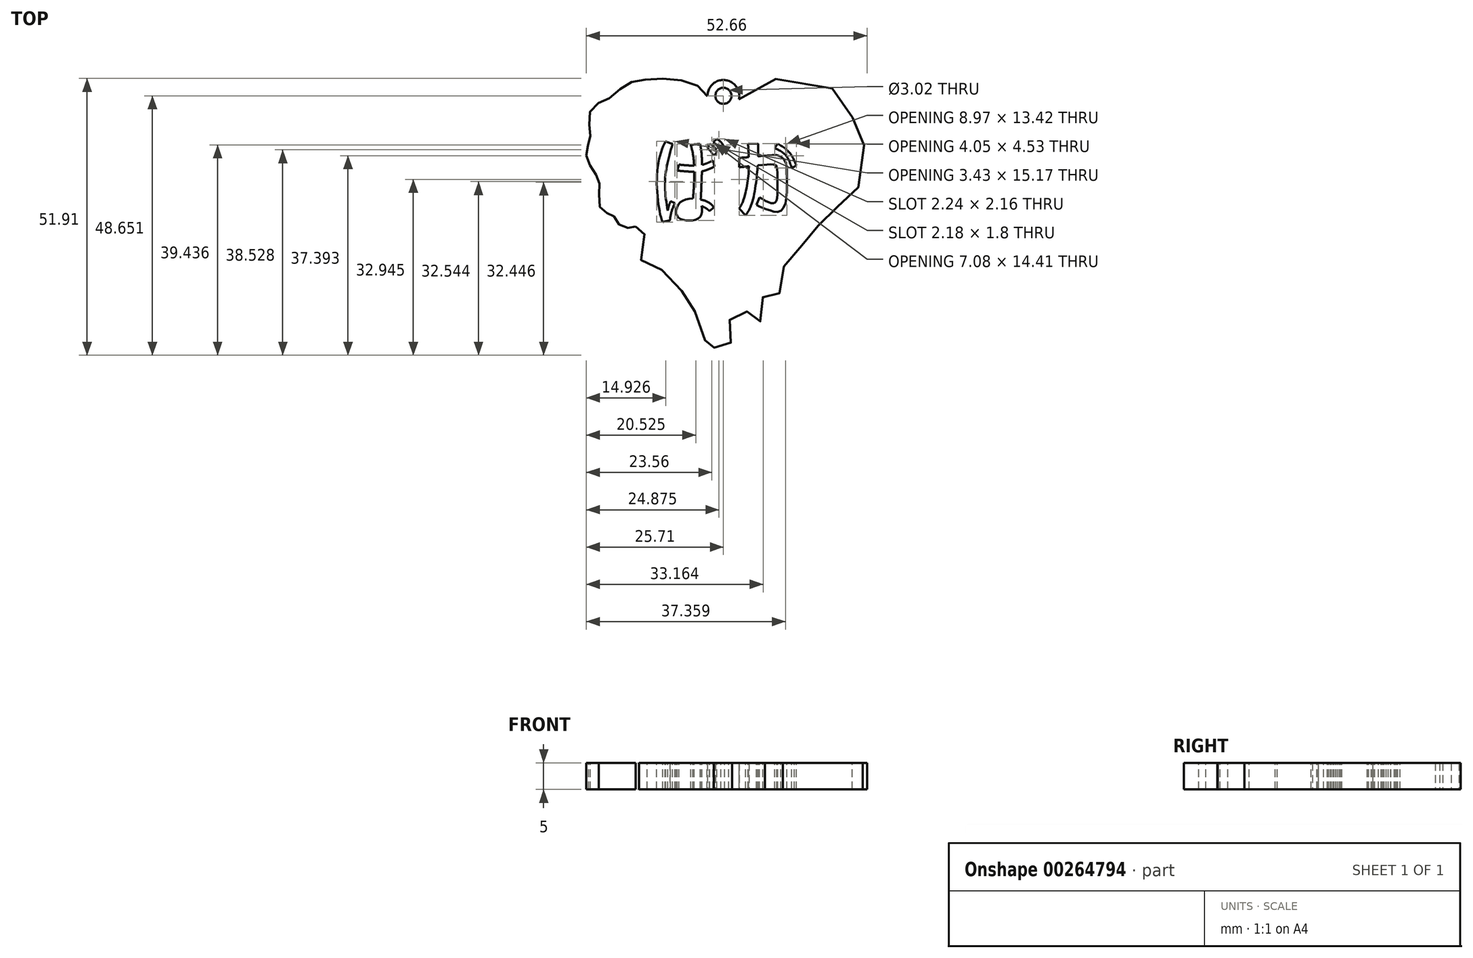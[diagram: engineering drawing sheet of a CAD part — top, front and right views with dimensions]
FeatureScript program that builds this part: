
annotation { "Feature Type Name" : "Feature", "Feature Type Description" : "" }
export const myFeature = defineFeature(function(context is Context, id is Id, definition is map)
    precondition{}
    {
        {
            var Q0;
            Q0=qCreatedBy(makeId("Top.planeOp"),FACE);
            var sketch = newSketch(context, id + "F0", { "sketchPlane" : qUnion([Q0])});
            skLineSegment(sketch, "E0", {"start": v(0.08, 15.96) * mm, "end": v(0.08, -29.04) * mm, "construction": true});
            skFitSpline(sketch, "E1", {"points": [v(0.08, 15.12) * mm, v(1.8, 15.96) * mm, v(5.58, 18.64) * mm, v(10.27, 20.57) * mm, v(19.75, 18.98) * mm, v(24.03, 15.96) * mm, v(24.45, 12.86) * mm, v(26.8, 11.1) * mm, v(26.13, 6.82) * mm, v(26.04, 2.12) * mm, v(23.27, -2.16) * mm, v(21.76, -2.5) * mm, v(21.1, -4.34) * mm, v(19.08, -6.1) * mm, v(17.82, -6.94) * mm, v(17.4, -9.03) * mm, v(15.64, -10.54) * mm, v(14.05, -10.96) * mm, v(13.55, -11.97) * mm, v(11.31, -14.7) * mm, v(10.84, -16.77) * mm, v(11.02, -19.08) * mm, v(9.42, -19.91) * mm, v(8.4, -19.08) * mm, v(7.52, -19.68) * mm, v(7.64, -22.23) * mm, v(7.7, -24.18) * mm, v(6.92, -24.96) * mm, v(6.21, -24.54) * mm, v(5.98, -25.01) * mm, v(5.09, -23.65) * mm, v(3.95, -23.12) * mm, v(3.15, -23.83) * mm, v(2.05, -24.06) * mm, v(1.07, -24.92) * mm, v(1.37, -27.18) * mm, v(1.6, -28.22) * mm, v(1.31, -29.31) * mm, v(0.68, -31) * mm, v(-1.46, -30.7) * mm, v(-1.93, -27.26) * mm, v(-2.64, -27.61) * mm, v(-3.35, -28.5) * mm, v(-4.3, -27.67) * mm, v(-5.2, -23.88) * mm, v(-5.67, -22.34) * mm, v(-6.74, -20.85) * mm, v(-7.62, -19.37) * mm, v(-10.41, -18.13) * mm, v(-11.48, -16) * mm, v(-12.13, -13.86) * mm, v(-14.5, -14.15) * mm, v(-15.75, -12.61) * mm, v(-15.51, -9.65) * mm, v(-15.04, -9) * mm, v(-14.33, -7.33) * mm, v(-14.5, -6.15) * mm, v(-16.46, -7.15) * mm], "startDerivative": vector(95.52, 38.59) * mm, "endDerivative": vector(-155.6, -97.2) * mm});
            skFitSpline(sketch, "E2", {"points": [v(-16.46, -7.15) * mm, v(-17.56, -7.42) * mm, v(-19.07, -7.15) * mm, v(-20.23, -5.85) * mm, v(-20.94, -4.84) * mm, v(-22.37, -4.47) * mm, v(-23.32, -2.82) * mm, v(-23.25, 0) * mm, v(-23.46, 1.56) * mm, v(-24.38, 3.32) * mm, v(-25.54, 5.33) * mm, v(-25.65, 7.1) * mm, v(-25.15, 9) * mm, v(-24.98, 10.83) * mm, v(-25.19, 13.83) * mm, v(-23.58, 15.97) * mm, v(-21.2, 17.06) * mm, v(-18.3, 19.45) * mm, v(-15.24, 20.33) * mm, v(-9.5, 20.5) * mm, v(-4.33, 18.86) * mm, v(-2.15, 16.14) * mm, v(-0.7, 15.1) * mm, v(0.08, 15.12) * mm], "startDerivative": vector(-33.79, -11.1) * mm, "endDerivative": vector(28.69, 5.55) * mm});
            skFitSpline(sketch, "E3", {"points": [v(-15.54, 7.18) * mm, v(-16.93, 6.43) * mm, v(-18.22, 6.03) * mm, v(-18.97, 4.49) * mm, v(-17.48, 2.5) * mm, v(-15.18, 1.6) * mm, v(-13.54, 0) * mm, v(-10.45, 0) * mm, v(-8.2, 0.55) * mm, v(-7.81, 0.5) * mm, v(-7.52, 0.56) * mm, v(-7.36, 1.37) * mm, v(-6.93, 1.67) * mm, v(-6.3, 2.5) * mm, v(-5.9, 2.96) * mm, v(-5.21, 3.13) * mm, v(-3.7, 4.49) * mm, v(-3.46, 7.08) * mm, v(-3.3, 9.72) * mm, v(-4.6, 11.37) * mm, v(-6.9, 10.92) * mm, v(-8.9, 8.87) * mm, v(-10.99, 8.82) * mm, v(-12.63, 8.57) * mm, v(-14.5, 8.18) * mm, v(-15.54, 7.18) * mm]});
            skFitSpline(sketch, "E4", {"points": [v(5.9, 10.84) * mm, v(4.72, 9.72) * mm, v(4.49, 8.06) * mm, v(5.44, 7.34) * mm, v(5.2, 5.8) * mm, v(6.27, 4.14) * mm, v(8.22, 3.6) * mm, v(9.82, 1.53) * mm, v(11.13, -0.54) * mm, v(12.61, -0.54) * mm, v(15.46, 1.06) * mm, v(17.47, 1.65) * mm, v(17.89, 4.2) * mm, v(15.93, 4.32) * mm, v(15.52, 7.17) * mm, v(14.92, 8.06) * mm, v(12.61, 8.47) * mm, v(11.25, 10.66) * mm, v(9.65, 10.66) * mm, v(6.86, 10.84) * mm, v(5.9, 10.84) * mm]});
            skCircle(sketch, "E5", {"center": v(0, 17.36) * mm, "radius": 2.97 * mm});
            skCircle(sketch, "E6", {"center": v(0, 17.36) * mm, "radius": 1.5 * mm});
            skSolve(sketch);
        }
        {
            var Q0;
            Q0=makeQuery(id+"F0.imprint","IMPRINT",FACE,{"disambiguationData":[TD([[makeQuery(id+"F0.imprint","IMPRINT",EDGE,{"derivedFrom":sQuery(id+"F0.wireOp",EDGE,"E1")}),-1.0]])]});
            var Q1;
            Q1=makeQuery(id+"F0.imprint","IMPRINT",FACE,{"disambiguationData":[TD([[makeQuery(id+"F0.imprint","IMPRINT",EDGE,{"derivedFrom":sQuery(id+"F0.wireOp",EDGE,"E3")}),-1.0]])]});
            var Q2;
            Q2=makeQuery(id+"F0.imprint","IMPRINT",FACE,{"disambiguationData":[TD([[makeQuery(id+"F0.imprint","IMPRINT",EDGE,{"derivedFrom":sQuery(id+"F0.wireOp",EDGE,"E6")}),-1.0]])]});
            var Q3;
            Q3=makeQuery(id+"F0.imprint","IMPRINT",FACE,{"disambiguationData":[TD([[makeQuery(id+"F0.imprint","IMPRINT",EDGE,{"derivedFrom":sQuery(id+"F0.wireOp",EDGE,"E3")}),1.0]])]});
            var Q4;
            Q4=makeQuery(id+"F0.imprint","IMPRINT",FACE,{"disambiguationData":[TD([[makeQuery(id+"F0.imprint","IMPRINT",EDGE,{"derivedFrom":sQuery(id+"F0.wireOp",EDGE,"E4")}),1.0]])]});
            extrude(context, id + "F1", {"entities" : qUnion([Q0, Q1, Q2, Q3, Q4]), "depth" : 5 * mm, "offsetDistance" : 25 * mm});
        }
        {
            var Q0;
            Q0=makeQuery(id+"F1.opExtrude","CAP_FACE",FACE,{"disambiguationData":[OSD([sQuery(id+"F0.wireOp",EDGE,"E1"),sQuery(id+"F0.wireOp",EDGE,"E2"),sQuery(id+"F0.wireOp",EDGE,"E5"),sQuery(id+"F0.wireOp",EDGE,"E6")])],"isStart":false});
            var sketch = newSketch(context, id + "F2", { "sketchPlane" : qUnion([Q0])});
            skLineSegment(sketch, "E7", {"start": v(-13.16, -6.33) * mm, "end": v(16.74, -6.33) * mm, "construction": true});
            skLineSegment(sketch, "E8", {"start": v(16.74, -6.33) * mm, "end": v(16.74, 9.26) * mm, "construction": true});
            skLineSegment(sketch, "E9", {"start": v(16.74, 9.26) * mm, "end": v(-13.16, 9.26) * mm, "construction": true});
            skLineSegment(sketch, "E10", {"start": v(-13.16, 9.26) * mm, "end": v(-13.16, -6.33) * mm, "construction": true});
            skFitSpline(sketch, "E11", {"points": [v(-10.8, 8.84) * mm, v(-11.93, 6.04) * mm, v(-12.5, 1.16) * mm, v(-12.07, -3.77) * mm, v(-11.36, -6.33) * mm], "startDerivative": vector(-6.02, -9.28) * mm, "endDerivative": vector(4.94, -9.57) * mm});
            skFitSpline(sketch, "E12", {"points": [v(-10.8, 8.84) * mm, v(-10.28, 8.58) * mm, v(-9.54, 8.35) * mm], "startDerivative": vector(1.05, -0.57) * mm, "endDerivative": vector(1.44, -0.4) * mm});
            skFitSpline(sketch, "E13", {"points": [v(-9.54, 8.35) * mm, v(-10.95, 1.3) * mm, v(-10.04, -6.07) * mm], "startDerivative": vector(-3.92, -13.91) * mm, "endDerivative": vector(2.94, -13.12) * mm});
            skFitSpline(sketch, "E14", {"points": [v(-10.04, -6.07) * mm, v(-11.36, -6.33) * mm], "startDerivative": vector(-1.2, -0.1) * mm, "endDerivative": vector(-1.54, -0.47) * mm});
            skFitSpline(sketch, "E15", {"points": [v(-10.04, -6.07) * mm, v(-9.7, -4.26) * mm, v(-9.07, -2.75) * mm], "startDerivative": vector(0.48, 3.62) * mm, "endDerivative": vector(1.47, 3) * mm});
            skFitSpline(sketch, "E16", {"points": [v(-9.07, -2.75) * mm, v(-9.9, -2.42) * mm], "startDerivative": vector(-0.82, 0.34) * mm, "endDerivative": vector(-0.82, 0.34) * mm});
            skFitSpline(sketch, "E17", {"points": [v(-9.9, -2.42) * mm, v(-10.04, -2.75) * mm, v(-10.44, -4.17) * mm], "startDerivative": vector(-0.43, -0.82) * mm, "endDerivative": vector(-0.48, -2.66) * mm});
            skFitSpline(sketch, "E18", {"points": [v(-6.12, 8.17) * mm, v(-5.62, 5.8) * mm, v(-5.5, 1.3) * mm, v(-5.95, -4.9) * mm], "startDerivative": vector(2.32, -8.67) * mm, "endDerivative": vector(-1.4, -15.69) * mm});
            skFitSpline(sketch, "E19", {"points": [v(-5.95, -4.9) * mm, v(-4.36, -4.9) * mm], "startDerivative": vector(1.3, 0) * mm, "endDerivative": vector(1.3, 0) * mm});
            skFitSpline(sketch, "E20", {"points": [v(-4.36, -4.9) * mm, v(-4.12, 0.56) * mm, v(-4.05, 5.87) * mm, v(-4.36, 8.36) * mm], "startDerivative": vector(0.46, 15.82) * mm, "endDerivative": vector(-2.5, 9.05) * mm, "construction": true});
            skFitSpline(sketch, "E21", {"points": [v(-4.36, 8.36) * mm, v(-6.12, 8.17) * mm], "startDerivative": vector(-1.47, -0.2) * mm, "endDerivative": vector(-1.47, -0.2) * mm});
            skFitSpline(sketch, "E22", {"points": [v(-4.36, -4.9) * mm, v(-5.37, -5.7) * mm, v(-7.44, -5.83) * mm, v(-8.67, -4.9) * mm, v(-8.37, -3.2) * mm, v(-7.14, -2.26) * mm, v(-5.72, -2.22) * mm, v(-4.28, -2.84) * mm, v(-3.01, -3.78) * mm], "startDerivative": vector(-6.42, -6.97) * mm, "endDerivative": vector(10.4, -8.5) * mm, "construction": true});
            skFitSpline(sketch, "E23", {"points": [v(-3.01, -3.78) * mm, v(-3.74, -4.55) * mm], "startDerivative": vector(-0.73, -0.77) * mm, "endDerivative": vector(-0.73, -0.77) * mm});
            skFitSpline(sketch, "E24", {"points": [v(-3.74, -4.55) * mm, v(-4.33, -4) * mm, v(-5.81, -3.31) * mm, v(-6.75, -3.25) * mm, v(-7.54, -4) * mm, v(-7.18, -4.56) * mm, v(-5.91, -4.42) * mm], "startDerivative": vector(-4.28, 4.04) * mm, "endDerivative": vector(9.33, 5.88) * mm, "construction": true});
            skFitSpline(sketch, "E25", {"points": [v(-8.33, 4.46) * mm, v(-5.5, 4.26) * mm, v(-3.73, 4.49) * mm, v(-1.93, 5.22) * mm], "startDerivative": vector(7.87, -0.77) * mm, "endDerivative": vector(5.76, 2.67) * mm});
            skFitSpline(sketch, "E26", {"points": [v(-8.33, 4.46) * mm, v(-8.66, 3.33) * mm], "startDerivative": vector(-0.34, -1.13) * mm, "endDerivative": vector(-0.34, -1.13) * mm});
            skFitSpline(sketch, "E27", {"points": [v(-8.66, 3.33) * mm, v(-5.47, 3.1) * mm, v(-3.5, 3.33) * mm, v(-1.65, 4.1) * mm], "startDerivative": vector(8.74, -0.85) * mm, "endDerivative": vector(6.05, 2.86) * mm});
            skFitSpline(sketch, "E28", {"points": [v(-1.65, 4.1) * mm, v(-1.93, 5.22) * mm], "startDerivative": vector(-0.28, 1.13) * mm, "endDerivative": vector(-0.28, 1.13) * mm});
            skFitSpline(sketch, "E29", {"points": [v(-4.36, -4.9) * mm, v(-5.37, -5.7) * mm, v(-7.44, -5.83) * mm, v(-8.67, -4.9) * mm, v(-8.37, -3.2) * mm, v(-7.14, -2.26) * mm, v(-5.5, -1.95) * mm, v(-4.25, -2.1) * mm, v(-3.16, -2.45) * mm, v(-2.1, -3.2) * mm, v(-1.8, -3.62) * mm], "startDerivative": vector(-7.64, -8.88) * mm, "endDerivative": vector(3.46, -6.08) * mm});
            skFitSpline(sketch, "E30", {"points": [v(-1.8, -3.62) * mm, v(-2.6, -4.24) * mm], "startDerivative": vector(-0.79, -0.62) * mm, "endDerivative": vector(-0.79, -0.62) * mm});
            skFitSpline(sketch, "E31", {"points": [v(-2.6, -4.24) * mm, v(-3.46, -3.62) * mm, v(-4.3, -3.2) * mm], "startDerivative": vector(-1.64, 1.3) * mm, "endDerivative": vector(-1.71, 0.72) * mm});
            skFitSpline(sketch, "E32", {"points": [v(-4.36, 8.36) * mm, v(-4.05, 5.87) * mm, v(-4.12, 0.56) * mm, v(-4.25, -2.1) * mm], "startDerivative": vector(1.32, -7.53) * mm, "endDerivative": vector(-0.4, -7.9) * mm});
            skFitSpline(sketch, "E33", {"points": [v(-4.36, -4.9) * mm, v(-4.25, -4.48) * mm, v(-4.25, -3.61) * mm, v(-4.3, -3.2) * mm], "startDerivative": vector(0.47, 1.25) * mm, "endDerivative": vector(-0.2, 1.27) * mm});
            skArc(sketch, "E34", {"start": v(-1.25, 6.67) * mm, "mid": v(-1.66, 7.7) * mm, "end": v(-2.58, 8.33) * mm});
            skFitSpline(sketch, "E35", {"points": [v(-1.25, 6.67) * mm, v(-1.87, 6.15) * mm], "startDerivative": vector(-0.62, -0.52) * mm, "endDerivative": vector(-0.62, -0.52) * mm});
            skFitSpline(sketch, "E36", {"points": [v(-2.58, 8.33) * mm, v(-3.05, 7.57) * mm], "startDerivative": vector(-0.47, -0.76) * mm, "endDerivative": vector(-0.47, -0.76) * mm});
            skArc(sketch, "E37", {"start": v(-1.87, 6.15) * mm, "mid": v(-2.36, 6.94) * mm, "end": v(-3.05, 7.57) * mm});
            skArc(sketch, "E38", {"start": v(-0.5, 7.03) * mm, "mid": v(-1.05, 7.95) * mm, "end": v(-1.91, 8.62) * mm});
            skArc(sketch, "E39", {"start": v(0.24, 7.5) * mm, "mid": v(-0.32, 8.51) * mm, "end": v(-1.2, 9.26) * mm});
            skFitSpline(sketch, "E40", {"points": [v(-1.2, 9.26) * mm, v(-1.91, 8.62) * mm], "startDerivative": vector(-0.71, -0.65) * mm, "endDerivative": vector(-0.71, -0.65) * mm});
            skFitSpline(sketch, "E41", {"points": [v(-0.5, 7.03) * mm, v(0.24, 7.5) * mm], "startDerivative": vector(0.73, 0.47) * mm, "endDerivative": vector(0.73, 0.47) * mm});
            skFitSpline(sketch, "E42", {"points": [v(-4.22, -1.58) * mm, v(-4.03, -3.6) * mm, v(-4.05, -4.62) * mm, v(-4.36, -5.36) * mm, v(-5.18, -5.88) * mm, v(-6.23, -6.05) * mm, v(-6.4, -6.05) * mm, v(-7.27, -5.97) * mm, v(-8.11, -5.74) * mm, v(-8.6, -5.26) * mm, v(-8.85, -4.5) * mm, v(-8.53, -3.2) * mm, v(-7.78, -2.4) * mm, v(-6.48, -1.95) * mm, v(-4.97, -1.95) * mm, v(-4.6, -2.04) * mm], "startDerivative": vector(2.38, -22.28) * mm, "endDerivative": vector(7.06, -2.12) * mm});
            skFitSpline(sketch, "E43", {"points": [v(4.63, 8.34) * mm, v(4.52, 4.27) * mm, v(3, -2.08) * mm, v(0.87, -4.98) * mm], "startDerivative": vector(-0.07, -11.9) * mm, "endDerivative": vector(-7.87, -8.24) * mm, "construction": true});
            skPoint(sketch, "E44.1.internal.snap0", {"position": v(1.8, -6.33) * mm});
            skFitSpline(sketch, "E44", {"points": [v(0.87, -4.98) * mm, v(1.8, -5.83) * mm], "startDerivative": vector(0.92, -0.85) * mm, "endDerivative": vector(0.92, -0.85) * mm});
            skFitSpline(sketch, "E45", {"points": [v(1.8, -5.83) * mm, v(4.33, -2.94) * mm, v(5.8, 4.22) * mm, v(5.9, 8.48) * mm], "startDerivative": vector(9.65, 7.85) * mm, "endDerivative": vector(-0.14, 12.43) * mm, "construction": true});
            skFitSpline(sketch, "E46", {"points": [v(5.9, 8.48) * mm, v(4.63, 8.34) * mm], "startDerivative": vector(-1.18, -0.14) * mm, "endDerivative": vector(-1.18, -0.14) * mm, "construction": true});
            skFitSpline(sketch, "E47", {"points": [v(2.97, 5.7) * mm, v(4.61, 5.8) * mm, v(5.89, 5.93) * mm, v(8.2, 6.17) * mm, v(10.5, 6.11) * mm, v(11.72, 4.7) * mm, v(11.91, 1.1) * mm, v(11.66, -2.7) * mm, v(10.57, -4.33) * mm, v(8.42, -3.96) * mm, v(6.8, -2.42) * mm], "startDerivative": vector(19.2, 1.37) * mm, "endDerivative": vector(-10.73, 17.37) * mm, "construction": true});
            skFitSpline(sketch, "E48", {"points": [v(6.8, -2.42) * mm, v(7.94, -1.93) * mm], "startDerivative": vector(1.23, 0.8) * mm, "endDerivative": vector(1.23, 0.8) * mm, "construction": true});
            skFitSpline(sketch, "E49", {"points": [v(7.94, -1.93) * mm, v(9.85, -2.83) * mm, v(10.48, -2.42) * mm, v(10.68, 1) * mm, v(10.5, 4.17) * mm, v(9.78, 4.46) * mm, v(5.8, 4.22) * mm], "startDerivative": vector(6.91, -12.73) * mm, "endDerivative": vector(-20.39, -1.62) * mm, "construction": true});
            skFitSpline(sketch, "E50", {"points": [v(2.97, 5.7) * mm, v(2.97, 4.27) * mm], "startDerivative": vector(0, -1.37) * mm, "endDerivative": vector(0, -1.37) * mm});
            skFitSpline(sketch, "E51", {"points": [v(2.97, 4.27) * mm, v(4.52, 4.27) * mm], "startDerivative": vector(1.28, 0) * mm, "endDerivative": vector(1.28, 0) * mm});
            skFitSpline(sketch, "E52", {"points": [v(10.02, 8.16) * mm, v(11.47, 7.22) * mm, v(12.54, 5.98) * mm, v(13.34, 4.07) * mm], "startDerivative": vector(4.64, -2.7) * mm, "endDerivative": vector(2, -5.68) * mm});
            skFitSpline(sketch, "E53", {"points": [v(10.02, 8.16) * mm, v(9.62, 7.56) * mm], "startDerivative": vector(-0.4, -0.6) * mm, "endDerivative": vector(-0.4, -0.6) * mm});
            skFitSpline(sketch, "E54", {"points": [v(9.62, 7.56) * mm, v(11.13, 6.72) * mm, v(12.1, 5.65) * mm, v(12.8, 3.84) * mm], "startDerivative": vector(4.78, -2.32) * mm, "endDerivative": vector(1.73, -5.46) * mm});
            skFitSpline(sketch, "E55", {"points": [v(12.8, 3.84) * mm, v(13.34, 4.07) * mm], "startDerivative": vector(0.54, 0.23) * mm, "endDerivative": vector(0.54, 0.23) * mm});
            skFitSpline(sketch, "E56", {"points": [v(13.34, 4.07) * mm, v(13.68, 4.32) * mm], "startDerivative": vector(0.33, 0.25) * mm, "endDerivative": vector(0.33, 0.25) * mm});
            skFitSpline(sketch, "E57", {"points": [v(13.68, 4.32) * mm, v(12.8, 6.15) * mm, v(11.68, 7.39) * mm, v(10.19, 8.37) * mm], "startDerivative": vector(-2.25, 5.53) * mm, "endDerivative": vector(-4.74, 2.8) * mm});
            skFitSpline(sketch, "E58", {"points": [v(10.19, 8.37) * mm, v(10.02, 8.16) * mm], "startDerivative": vector(-0.16, -0.2) * mm, "endDerivative": vector(-0.16, -0.2) * mm});
            skFitSpline(sketch, "E59", {"points": [v(9.45, 4.46) * mm, v(10.02, 3.96) * mm, v(10.14, 0.9) * mm, v(9.98, -2.28) * mm, v(9.32, -2.8) * mm], "startDerivative": vector(4.1, -2.01) * mm, "endDerivative": vector(-4.46, -1.87) * mm, "construction": true});
            skFitSpline(sketch, "E60", {"points": [v(9.32, -2.8) * mm, v(7.97, -2.36) * mm, v(6.75, -1.68) * mm], "startDerivative": vector(-2.76, 0.73) * mm, "endDerivative": vector(-2.38, 1.49) * mm, "construction": true});
            skFitSpline(sketch, "E61", {"points": [v(6.75, -1.68) * mm, v(6.2, -3.12) * mm], "startDerivative": vector(-0.56, -1.43) * mm, "endDerivative": vector(-0.56, -1.43) * mm, "construction": true});
            skFitSpline(sketch, "E62", {"points": [v(6.2, -3.12) * mm, v(7.5, -3.74) * mm, v(8.97, -4.22) * mm], "startDerivative": vector(2.17, -1.42) * mm, "endDerivative": vector(3, -1.2) * mm, "construction": true});
            skFitSpline(sketch, "E63", {"points": [v(2.97, 5.7) * mm, v(5.89, 5.93) * mm, v(8.2, 6.17) * mm, v(10.5, 6.11) * mm, v(11.72, 4.7) * mm, v(11.91, 1.1) * mm, v(11.66, -2.7) * mm, v(10.57, -4.33) * mm, v(8.97, -4.22) * mm, v(7.5, -3.74) * mm, v(6.2, -3.12) * mm], "startDerivative": vector(26.47, 2.28) * mm, "endDerivative": vector(-16.18, 8.31) * mm});
            skFitSpline(sketch, "E64", {"points": [v(6.2, -3.12) * mm, v(6.75, -1.68) * mm], "startDerivative": vector(0.56, 1.43) * mm, "endDerivative": vector(0.56, 1.43) * mm});
            skFitSpline(sketch, "E65", {"points": [v(6.75, -1.68) * mm, v(7.97, -2.36) * mm, v(9.32, -2.8) * mm, v(9.98, -2.28) * mm, v(10.14, 0.9) * mm, v(10.02, 3.96) * mm, v(9.45, 4.46) * mm, v(5.8, 4.22) * mm], "startDerivative": vector(9.4, -5.5) * mm, "endDerivative": vector(-22.2, -2.9) * mm});
            skFitSpline(sketch, "E66", {"points": [v(6.53, 8.37) * mm, v(6.55, 5.99) * mm, v(6.45, 4.3) * mm, v(5.48, -2.38) * mm, v(4.19, -5.06) * mm], "startDerivative": vector(0.2, -12.04) * mm, "endDerivative": vector(-5.84, -8.77) * mm});
            skFitSpline(sketch, "E67", {"points": [v(6.53, 8.37) * mm, v(4.63, 8.34) * mm], "startDerivative": vector(-1.82, -0.02) * mm, "endDerivative": vector(-1.82, -0.02) * mm});
            skFitSpline(sketch, "E68", {"points": [v(4.63, 8.34) * mm, v(4.63, 1.7) * mm, v(3.52, -2.8) * mm, v(2.97, -3.8) * mm], "startDerivative": vector(1.04, -15.91) * mm, "endDerivative": vector(-2.8, -4.44) * mm});
            skFitSpline(sketch, "E69", {"points": [v(2.97, -3.8) * mm, v(4.19, -5.06) * mm], "startDerivative": vector(1.22, -1.26) * mm, "endDerivative": vector(1.22, -1.26) * mm});
            skFitSpline(sketch, "E70", {"points": [v(5.8, 4.22) * mm, v(4.78, 4.13) * mm, v(3, 3.96) * mm], "startDerivative": vector(-2.2, -0.2) * mm, "endDerivative": vector(-3.36, -0.32) * mm});
            skFitSpline(sketch, "E71", {"points": [v(3, 3.96) * mm, v(2.97, 4.27) * mm], "startDerivative": vector(-0.02, 0.3) * mm, "endDerivative": vector(-0.02, 0.3) * mm});
            skSolve(sketch);
        }
        {
            var Q0;
            Q0=makeQuery(id+"F2.imprint","IMPRINT",FACE,{"disambiguationData":[TD([[makeQuery(id+"F2.imprint","IMPRINT",EDGE,{"derivedFrom":sQuery(id+"F2.wireOp",EDGE,"E11")}),1.0]])]});
            var Q1;
            {var subQ0=sQuery(id+"F2.wireOp",EDGE,"E15");Q1=makeQuery(id+"F2.imprint","IMPRINT",FACE,{"disambiguationData":[TD([[makeQuery(id+"F2.imprint","IMPRINT",EDGE,{"derivedFrom":subQ0}),1.0]])]});}
            var Q2;
            {var subQ0=sQuery(id+"F2.wireOp",EDGE,"E24");var subQ1=sQuery(id+"F2.wireOp",EDGE,"E18");var subQ2=makeQuery(id+"F2.imprint","INTERSECT",VERTEX,{"disambiguationData":[OD(0.0)],"derivedFrom":[subQ1,subQ0]});Q2=makeQuery(id+"F2.imprint","IMPRINT",FACE,{"disambiguationData":[TD([[makeQuery(id+"F2.imprint","IMPRINT",EDGE,{"disambiguationData":[TD([[subQ2,1.0]])],"derivedFrom":subQ1}),-1.0]])]});}
            var Q3;
            {var subQ0=sQuery(id+"F2.wireOp",EDGE,"E19");Q3=makeQuery(id+"F2.imprint","IMPRINT",FACE,{"disambiguationData":[TD([[makeQuery(id+"F2.imprint","IMPRINT",EDGE,{"derivedFrom":subQ0}),-1.0]])]});}
            var Q4;
            {var subQ1=sQuery(id+"F2.wireOp",EDGE,"E19");Q4=makeQuery(id+"F2.imprint","IMPRINT",FACE,{"disambiguationData":[TD([[makeQuery(id+"F2.imprint","IMPRINT",EDGE,{"derivedFrom":subQ1}),1.0]])]});}
            var Q5;
            {var subQ0=sQuery(id+"F2.wireOp",EDGE,"E22");var subQ1=sQuery(id+"F2.wireOp",EDGE,"E18");var subQ2=makeQuery(id+"F2.imprint","INTERSECT",VERTEX,{"derivedFrom":[subQ1,subQ0]});Q5=makeQuery(id+"F2.imprint","IMPRINT",FACE,{"disambiguationData":[TD([[makeQuery(id+"F2.imprint","IMPRINT",EDGE,{"disambiguationData":[TD([[subQ2,-1.0]])],"derivedFrom":subQ1}),1.0]])]});}
            var Q6;
            {var subQ5=sQuery(id+"F2.wireOp",EDGE,"E23");Q6=makeQuery(id+"F2.imprint","IMPRINT",FACE,{"disambiguationData":[TD([[makeQuery(id+"F2.imprint","IMPRINT",EDGE,{"derivedFrom":subQ5}),-1.0]])]});}
            var Q7;
            {var subQ0=sQuery(id+"F2.wireOp",EDGE,"E27");var subQ1=sQuery(id+"F2.wireOp",EDGE,"E18");var subQ2=makeQuery(id+"F2.imprint","INTERSECT",VERTEX,{"derivedFrom":[subQ1,subQ0]});Q7=makeQuery(id+"F2.imprint","IMPRINT",FACE,{"disambiguationData":[TD([[makeQuery(id+"F2.imprint","IMPRINT",EDGE,{"disambiguationData":[TD([[subQ2,-1.0]])],"derivedFrom":subQ1}),1.0]])]});}
            var Q8;
            {var subQ0=sQuery(id+"F2.wireOp",EDGE,"E25");var subQ1=sQuery(id+"F2.wireOp",EDGE,"E18");var subQ2=makeQuery(id+"F2.imprint","INTERSECT",VERTEX,{"derivedFrom":[subQ1,subQ0]});Q8=makeQuery(id+"F2.imprint","IMPRINT",FACE,{"disambiguationData":[TD([[makeQuery(id+"F2.imprint","IMPRINT",EDGE,{"disambiguationData":[TD([[subQ2,-1.0]])],"derivedFrom":subQ1}),1.0]])]});}
            var Q9;
            {var subQ5=sQuery(id+"F2.wireOp",EDGE,"E26");Q9=makeQuery(id+"F2.imprint","IMPRINT",FACE,{"disambiguationData":[TD([[makeQuery(id+"F2.imprint","IMPRINT",EDGE,{"derivedFrom":subQ5}),1.0]])]});}
            var Q10;
            {var subQ0=sQuery(id+"F2.wireOp",EDGE,"E21");Q10=makeQuery(id+"F2.imprint","IMPRINT",FACE,{"disambiguationData":[TD([[makeQuery(id+"F2.imprint","IMPRINT",EDGE,{"derivedFrom":subQ0}),1.0]])]});}
            var Q11;
            {var subQ5=sQuery(id+"F2.wireOp",EDGE,"E28");Q11=makeQuery(id+"F2.imprint","IMPRINT",FACE,{"disambiguationData":[TD([[makeQuery(id+"F2.imprint","IMPRINT",EDGE,{"derivedFrom":subQ5}),1.0]])]});}
            var Q12;
            {var subQ1=sQuery(id+"F2.wireOp",EDGE,"E30");Q12=makeQuery(id+"F2.imprint","IMPRINT",FACE,{"disambiguationData":[TD([[makeQuery(id+"F2.imprint","IMPRINT",EDGE,{"derivedFrom":subQ1}),-1.0]])]});}
            var Q13;
            Q13=makeQuery(id+"F2.imprint","IMPRINT",FACE,{"disambiguationData":[TD([[makeQuery(id+"F2.imprint","IMPRINT",EDGE,{"derivedFrom":sQuery(id+"F2.wireOp",EDGE,"b741c950-454b-47e5-acc8-c98bc9226f96")}),1.0]])]});
            var Q14;
            Q14=makeQuery(id+"F2.imprint","IMPRINT",FACE,{"disambiguationData":[TD([[makeQuery(id+"F2.imprint","IMPRINT",EDGE,{"derivedFrom":sQuery(id+"F2.wireOp",EDGE,"d5f50271-82d2-4fe2-802b-595531122f13")}),1.0]])]});
            var Q15;
            Q15=makeQuery(id+"F2.imprint","IMPRINT",FACE,{"disambiguationData":[TD([[makeQuery(id+"F2.imprint","IMPRINT",EDGE,{"derivedFrom":sQuery(id+"F2.wireOp",EDGE,"E34")}),1.0]])]});
            var Q16;
            Q16=makeQuery(id+"F2.imprint","IMPRINT",FACE,{"disambiguationData":[TD([[makeQuery(id+"F2.imprint","IMPRINT",EDGE,{"derivedFrom":sQuery(id+"F2.wireOp",EDGE,"E38")}),-1.0]])]});
            var Q17;
            {var subQ0=sQuery(id+"F2.wireOp",EDGE,"E33");Q17=makeQuery(id+"F2.imprint","IMPRINT",FACE,{"disambiguationData":[TD([[makeQuery(id+"F2.imprint","IMPRINT",EDGE,{"derivedFrom":subQ0}),-1.0]])]});}
            extrude(context, id + "F3", {"entities" : qUnion([Q0, Q1, Q2, Q3, Q4, Q5, Q6, Q7, Q8, Q9, Q10, Q11, Q12, Q13, Q14, Q15, Q16, Q17]), "operationType" : NewBodyOperationType.REMOVE, "oppositeDirection" : true, "depth" : 25 * mm, "offsetDistance" : 25 * mm});
        }
        {
            var Q0;
            {var subQ1=sQuery(id+"F2.wireOp",EDGE,"E44");Q0=makeQuery(id+"F2.imprint","IMPRINT",FACE,{"disambiguationData":[TD([[makeQuery(id+"F2.imprint","IMPRINT",EDGE,{"derivedFrom":subQ1}),1.0]])]});}
            var Q1;
            {var subQ0=sQuery(id+"F2.wireOp",EDGE,"E46");Q1=makeQuery(id+"F2.imprint","IMPRINT",FACE,{"disambiguationData":[TD([[makeQuery(id+"F2.imprint","IMPRINT",EDGE,{"derivedFrom":subQ0}),1.0]])]});}
            var Q2;
            {var subQ4=sQuery(id+"F2.wireOp",EDGE,"E50");Q2=makeQuery(id+"F2.imprint","IMPRINT",FACE,{"disambiguationData":[TD([[makeQuery(id+"F2.imprint","IMPRINT",EDGE,{"derivedFrom":subQ4}),1.0]])]});}
            var Q3;
            {var subQ4=sQuery(id+"F2.wireOp",EDGE,"E48");Q3=makeQuery(id+"F2.imprint","IMPRINT",FACE,{"disambiguationData":[TD([[makeQuery(id+"F2.imprint","IMPRINT",EDGE,{"derivedFrom":subQ4}),-1.0]])]});}
            var Q4;
            Q4=makeQuery(id+"F2.imprint","IMPRINT",FACE,{"disambiguationData":[TD([[makeQuery(id+"F2.imprint","IMPRINT",EDGE,{"derivedFrom":sQuery(id+"F2.wireOp",EDGE,"E52")}),-1.0]])]});
            var Q5;
            Q5=makeQuery(id+"F2.imprint","IMPRINT",FACE,{"disambiguationData":[TD([[makeQuery(id+"F2.imprint","IMPRINT",EDGE,{"derivedFrom":sQuery(id+"F2.wireOp",EDGE,"E52")}),1.0]])]});
            var Q6;
            {var subQ4=sQuery(id+"F2.wireOp",EDGE,"E64");Q6=makeQuery(id+"F2.imprint","IMPRINT",FACE,{"disambiguationData":[TD([[makeQuery(id+"F2.imprint","IMPRINT",EDGE,{"derivedFrom":subQ4}),-1.0]])]});}
            extrude(context, id + "F4", {"entities" : qUnion([Q0, Q1, Q2, Q3, Q4, Q5, Q6]), "operationType" : NewBodyOperationType.REMOVE, "oppositeDirection" : true, "depth" : 25 * mm, "offsetDistance" : 25 * mm});
        }
        {
            var Q0;
            {var subQ1=sQuery(id+"F2.wireOp",EDGE,"E63");var subQ7=sQuery(id+"F2.wireOp",EDGE,"E68");var subQ8=makeQuery(id+"F2.imprint","INTERSECT",VERTEX,{"derivedFrom":[subQ1,subQ7]});Q0=makeQuery(id+"F2.imprint","IMPRINT",FACE,{"disambiguationData":[TD([[makeQuery(id+"F2.imprint","IMPRINT",EDGE,{"disambiguationData":[TD([[subQ8,-1.0]])],"derivedFrom":subQ1}),-1.0]])]});}
            var Q1;
            {var subQ5=sQuery(id+"F2.wireOp",EDGE,"E67");Q1=makeQuery(id+"F2.imprint","IMPRINT",FACE,{"disambiguationData":[TD([[makeQuery(id+"F2.imprint","IMPRINT",EDGE,{"derivedFrom":subQ5}),1.0]])]});}
            var Q2;
            {var subQ0=sQuery(id+"F2.wireOp",EDGE,"E69");Q2=makeQuery(id+"F2.imprint","IMPRINT",FACE,{"disambiguationData":[TD([[makeQuery(id+"F2.imprint","IMPRINT",EDGE,{"derivedFrom":subQ0}),1.0]])]});}
            extrude(context, id + "F5", {"entities" : qUnion([Q0, Q1, Q2]), "operationType" : NewBodyOperationType.REMOVE, "oppositeDirection" : true, "depth" : 25 * mm, "offsetDistance" : 25 * mm});
        }
    });
